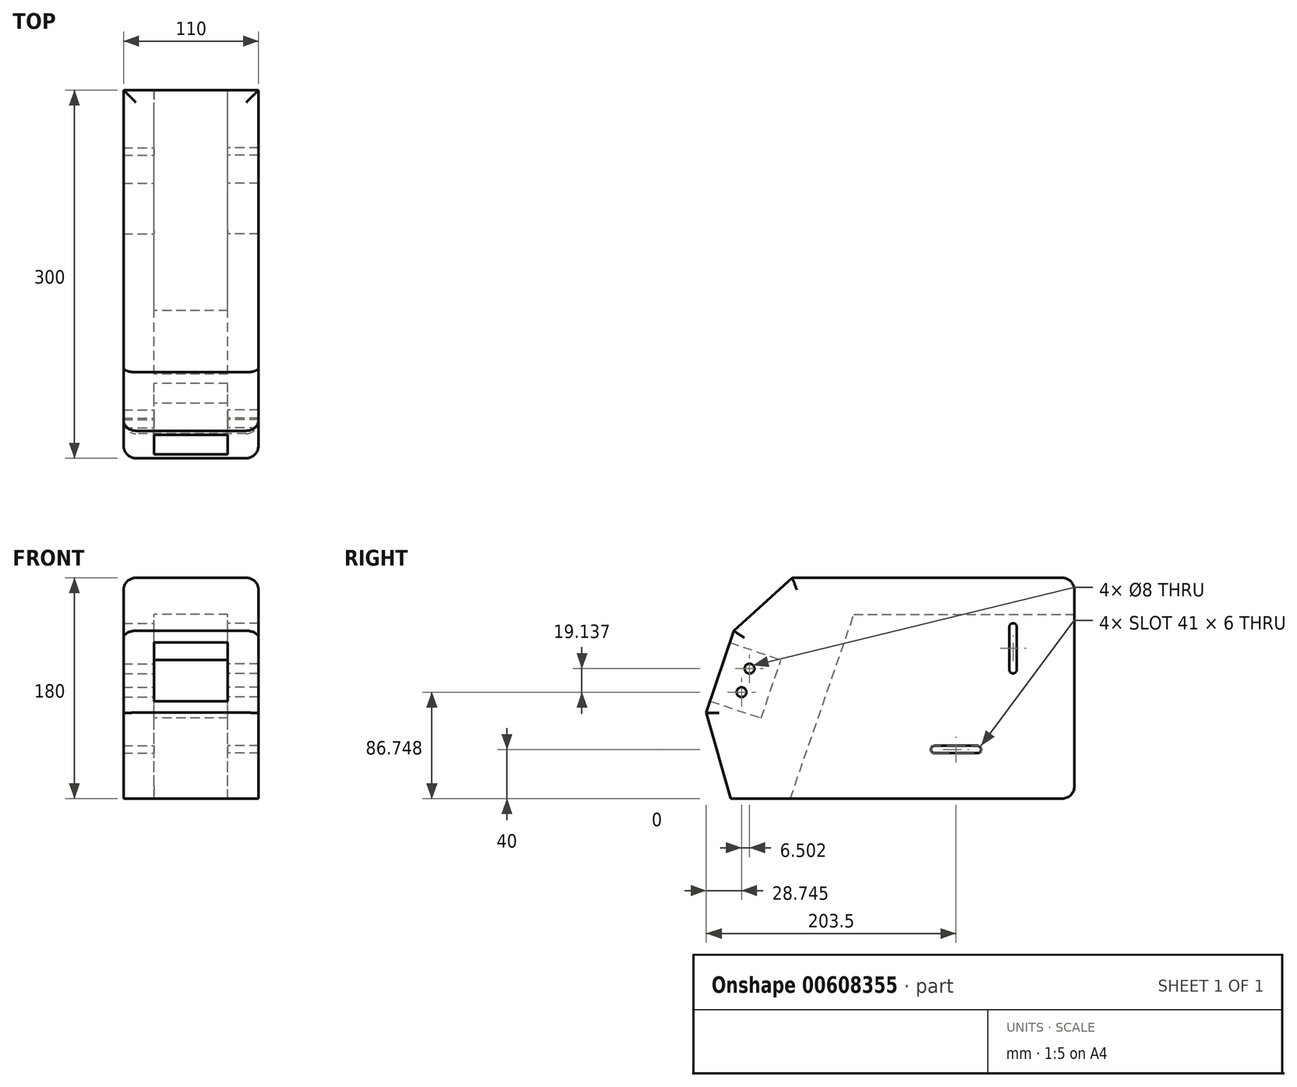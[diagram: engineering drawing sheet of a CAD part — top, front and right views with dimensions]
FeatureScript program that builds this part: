
annotation { "Feature Type Name" : "Feature", "Feature Type Description" : "" }
export const myFeature = defineFeature(function(context is Context, id is Id, definition is map)
    precondition{}
    {
        {
            var Q0;
            Q0=qCreatedBy(makeId("Right.planeOp"),FACE);
            var sketch = newSketch(context, id + "F0", { "sketchPlane" : qUnion([Q0])});
            skLineSegment(sketch, "E0.bottom", {"start": v(150, -90) * mm, "end": v(-150, -90) * mm, "construction": true});
            skLineSegment(sketch, "E0.top", {"start": v(150, 90) * mm, "end": v(-150, 90) * mm, "construction": true});
            skLineSegment(sketch, "E0.left", {"start": v(150, -90) * mm, "end": v(150, 90) * mm, "construction": true});
            skLineSegment(sketch, "E0.right", {"start": v(-150, -90) * mm, "end": v(-150, 90) * mm, "construction": true});
            skPoint(sketch, "E0.middle", {"position": v(0, 0) * mm});
            skLineSegment(sketch, "E1", {"start": v(-150, -20) * mm, "end": v(-113.22, 90) * mm, "construction": true});
            skLineSegment(sketch, "E2", {"start": v(-150, -20) * mm, "end": v(-92.1, -20) * mm, "construction": true});
            skLineSegment(sketch, "E3", {"start": v(-105.33, -24.4) * mm, "end": v(-89.02, 22.87) * mm});
            skLineSegment(sketch, "E4", {"start": v(-127.67, 46.79) * mm, "end": v(-130.84, 37.3) * mm});
            skLineSegment(sketch, "E5", {"start": v(-130.84, 37.3) * mm, "end": v(-89.02, 22.87) * mm});
            skLineSegment(sketch, "E6", {"start": v(-150, -20) * mm, "end": v(-146.83, -10.52) * mm});
            skLineSegment(sketch, "E7", {"start": v(-146.83, -10.52) * mm, "end": v(-105.33, -24.4) * mm});
            skLineSegment(sketch, "E8", {"start": v(-109.93, 30.09) * mm, "end": v(-126.08, -17.45) * mm, "construction": true});
            skCircle(sketch, "E9", {"center": v(-114.75, 15.89) * mm, "radius": 4 * mm, "construction": true});
            skCircle(sketch, "E10", {"center": v(-121.25, -3.25) * mm, "radius": 4 * mm, "construction": true});
            skLineSegment(sketch, "E11", {"start": v(-150, -20) * mm, "end": v(-130, -90) * mm});
            skLineSegment(sketch, "E12", {"start": v(-130, -90) * mm, "end": v(-81.49, -90) * mm});
            skLineSegment(sketch, "E13", {"start": v(-81.49, -90) * mm, "end": v(-29.72, 60) * mm});
            skLineSegment(sketch, "E14", {"start": v(-29.72, 60) * mm, "end": v(150, 60) * mm});
            skLineSegment(sketch, "E15", {"start": v(150, 60) * mm, "end": v(150, 90) * mm});
            skLineSegment(sketch, "E16", {"start": v(-127.67, 46.79) * mm, "end": v(-80, 90) * mm});
            skLineSegment(sketch, "E17", {"start": v(-80, 90) * mm, "end": v(150, 90) * mm});
            skLineSegment(sketch, "E18", {"start": v(-29.72, 60) * mm, "end": v(-19.36, 90) * mm});
            skLineSegment(sketch, "E19", {"start": v(-19.36, 90) * mm, "end": v(-24.54, 75) * mm});
            skSolve(sketch);
        }
        {
            var Q0;
            Q0 = qSketchRegion(id + "F0", true);
            extrude(context, id + "F1", {"entities" : qUnion([Q0]), "endBound" : BoundingType.SYMMETRIC, "depth" : 60 * mm, "offsetDistance" : 25 * mm});
        }
        {
            var Q0;
            Q0=makeQuery(id+"F1.opExtrude","CAP_FACE",FACE,{"disambiguationData":[OSD([sQuery(id+"F0.wireOp",EDGE,"E3"),sQuery(id+"F0.wireOp",EDGE,"E4"),sQuery(id+"F0.wireOp",EDGE,"E5"),sQuery(id+"F0.wireOp",EDGE,"E6"),sQuery(id+"F0.wireOp",EDGE,"E7"),sQuery(id+"F0.wireOp",EDGE,"E11"),sQuery(id+"F0.wireOp",EDGE,"E12"),sQuery(id+"F0.wireOp",EDGE,"E13"),sQuery(id+"F0.wireOp",EDGE,"E14"),sQuery(id+"F0.wireOp",EDGE,"E15"),sQuery(id+"F0.wireOp",EDGE,"E16"),sQuery(id+"F0.wireOp",EDGE,"E17")])],"isStart":false});
            var sketch = newSketch(context, id + "F2", { "sketchPlane" : qUnion([Q0])});
            skLineSegment(sketch, "E20", {"start": v(-127.67, 46.79) * mm, "end": v(-80, 90) * mm});
            skLineSegment(sketch, "E21", {"start": v(-80, 90) * mm, "end": v(150, 90) * mm});
            skLineSegment(sketch, "E22", {"start": v(150, -90) * mm, "end": v(-130, -90) * mm});
            skLineSegment(sketch, "E23", {"start": v(-130, -90) * mm, "end": v(-150, -20) * mm});
            skLineSegment(sketch, "E24", {"start": v(-150, -20) * mm, "end": v(-127.67, 46.79) * mm});
            skLineSegment(sketch, "E25", {"start": v(36, -50) * mm, "end": v(71, -50) * mm, "construction": true});
            skLineSegment(sketch, "E26", {"start": v(71, -50) * mm, "end": v(100, -50) * mm, "construction": true});
            skLineSegment(sketch, "E27", {"start": v(100, -50) * mm, "end": v(100, 15) * mm, "construction": true});
            skLineSegment(sketch, "E28", {"start": v(100, 15) * mm, "end": v(100, 50) * mm, "construction": true});
            skLineSegment(sketch, "E29", {"start": v(150, 90) * mm, "end": v(150, -90) * mm});
            skArc(sketch, "E30.0.startCap", {"start": v(103, 15) * mm, "mid": v(100, 12) * mm, "end": v(97, 15) * mm});
            skArc(sketch, "E30.0.endCap", {"start": v(97, 50) * mm, "mid": v(100, 53) * mm, "end": v(103, 50) * mm});
            skLineSegment(sketch, "E30.0.left", {"start": v(97, 15) * mm, "end": v(97, 50) * mm});
            skLineSegment(sketch, "E30.0.right", {"start": v(103, 15) * mm, "end": v(103, 50) * mm});
            skArc(sketch, "E31.0.startCap", {"start": v(36, -53) * mm, "mid": v(33, -50) * mm, "end": v(36, -47) * mm});
            skArc(sketch, "E31.0.endCap", {"start": v(71, -47) * mm, "mid": v(74, -50) * mm, "end": v(71, -53) * mm});
            skLineSegment(sketch, "E31.0.left", {"start": v(36, -47) * mm, "end": v(71, -47) * mm});
            skLineSegment(sketch, "E31.0.right", {"start": v(36, -53) * mm, "end": v(71, -53) * mm});
            skCircle(sketch, "E32.0", {"center": v(-114.75, 15.89) * mm, "radius": 4 * mm});
            skCircle(sketch, "E32.1", {"center": v(-121.25, -3.25) * mm, "radius": 4 * mm});
            skSolve(sketch);
        }
        {
            var Q0;
            Q0 = qSketchRegion(id + "F2", true);
            extrude(context, id + "F3", {"entities" : qUnion([Q0]), "operationType" : NewBodyOperationType.ADD, "depth" : 25 * mm, "offsetDistance" : 25 * mm});
        }
        {
            var Q0;
            Q0=makeQuery(id+"F1.opExtrude","CAP_FACE",FACE,{"disambiguationData":[OSD([sQuery(id+"F0.wireOp",EDGE,"E3"),sQuery(id+"F0.wireOp",EDGE,"E4"),sQuery(id+"F0.wireOp",EDGE,"E5"),sQuery(id+"F0.wireOp",EDGE,"E6"),sQuery(id+"F0.wireOp",EDGE,"E7"),sQuery(id+"F0.wireOp",EDGE,"E11"),sQuery(id+"F0.wireOp",EDGE,"E12"),sQuery(id+"F0.wireOp",EDGE,"E13"),sQuery(id+"F0.wireOp",EDGE,"E14"),sQuery(id+"F0.wireOp",EDGE,"E15"),sQuery(id+"F0.wireOp",EDGE,"E16"),sQuery(id+"F0.wireOp",EDGE,"E17")])],"isStart":true});
            var sketch = newSketch(context, id + "F4", { "sketchPlane" : qUnion([Q0])});
            skLineSegment(sketch, "E33.0.0", {"start": v(127.67, 46.79) * mm, "end": v(150, -20) * mm});
            skLineSegment(sketch, "E33.0.1", {"start": v(150, -20) * mm, "end": v(130, -90) * mm});
            skLineSegment(sketch, "E33.0.2", {"start": v(130, -90) * mm, "end": v(-150, -90) * mm});
            skLineSegment(sketch, "E33.0.3", {"start": v(-150, -90) * mm, "end": v(-150, 90) * mm});
            skLineSegment(sketch, "E33.0.4", {"start": v(-150, 90) * mm, "end": v(80, 90) * mm});
            skLineSegment(sketch, "E33.0.5", {"start": v(80, 90) * mm, "end": v(127.67, 46.79) * mm});
            skLineSegment(sketch, "E34.0", {"start": v(-103, 15) * mm, "end": v(-103, 50) * mm});
            skArc(sketch, "E34.1", {"start": v(-97, 50) * mm, "mid": v(-100, 53) * mm, "end": v(-103, 50) * mm});
            skLineSegment(sketch, "E34.2", {"start": v(-97, 15) * mm, "end": v(-97, 50) * mm});
            skArc(sketch, "E34.3", {"start": v(-103, 15) * mm, "mid": v(-100, 12) * mm, "end": v(-97, 15) * mm});
            skLineSegment(sketch, "E34.4", {"start": v(-36, -47) * mm, "end": v(-71, -47) * mm});
            skLineSegment(sketch, "E34.5", {"start": v(-36, -53) * mm, "end": v(-71, -53) * mm});
            skArc(sketch, "E34.6", {"start": v(-71, -47) * mm, "mid": v(-74, -50) * mm, "end": v(-71, -53) * mm});
            skArc(sketch, "E34.7", {"start": v(-36, -53) * mm, "mid": v(-33, -50) * mm, "end": v(-36, -47) * mm});
            skSolve(sketch);
        }
        {
            var Q0;
            Q0=makeQuery(id+"F4.imprint","IMPRINT",FACE,{"disambiguationData":[TD([[makeQuery(id+"F4.imprint","IMPRINT",EDGE,{"derivedFrom":sQuery(id+"F4.wireOp",EDGE,"E34.0")}),1.0]])]});
            var Q1;
            {var subQ7=sQuery(id+"F4.wireOp",EDGE,"E33.0.1");Q1=makeQuery(id+"F4.imprint","IMPRINT",FACE,{"disambiguationData":[TD([[makeQuery(id+"F4.imprint","IMPRINT",EDGE,{"derivedFrom":subQ7}),-1.0]])]});}
            var Q2;
            Q2=makeQuery(id+"F4.imprint","IMPRINT",FACE,{"disambiguationData":[TD([[makeQuery(id+"F4.imprint","IMPRINT",EDGE,{"derivedFrom":makeQuery(id+"F1.opExtrude","CAP_EDGE",EDGE,{"disambiguationData":[OSD([sQuery(id+"F0.wireOp",EDGE,"E3")])],"isStart":true})}),-1.0]])]});
            extrude(context, id + "F5", {"entities" : qUnion([Q0, Q1, Q2]), "operationType" : NewBodyOperationType.ADD, "depth" : 25 * mm, "offsetDistance" : 25 * mm});
        }
        {
            var Q0;
            Q0=makeQuery(id+"F3.opExtrude","CAP_EDGE",EDGE,{"disambiguationData":[OSD([sQuery(id+"F2.wireOp",EDGE,"E21")])],"isStart":false});
            var Q1;
            Q1=makeQuery(id+"F3.opExtrude","CAP_EDGE",EDGE,{"disambiguationData":[OSD([sQuery(id+"F2.wireOp",EDGE,"E20")])],"isStart":false});
            var Q2;
            Q2=makeQuery(id+"F3.opExtrude","CAP_EDGE",EDGE,{"disambiguationData":[OSD([sQuery(id+"F2.wireOp",EDGE,"E23")])],"isStart":false});
            var Q3;
            Q3=makeQuery(id+"F5.opExtrude","CAP_EDGE",EDGE,{"disambiguationData":[OSD([sQuery(id+"F4.wireOp",EDGE,"E33.0.1")])],"isStart":false});
            var Q4;
            Q4=makeQuery(id+"F5.opExtrude","CAP_EDGE",EDGE,{"disambiguationData":[OSD([sQuery(id+"F4.wireOp",EDGE,"E33.0.5")])],"isStart":false});
            var Q5;
            Q5=makeQuery(id+"F5.opExtrude","CAP_EDGE",EDGE,{"disambiguationData":[OSD([sQuery(id+"F4.wireOp",EDGE,"E33.0.4")])],"isStart":false});
            var Q6;
            Q6=makeQuery(id+"F5.boolean.opBoolean","MERGE",EDGE,{"derivedFrom":[makeQuery(id+"F3.boolean.opBoolean","MERGE",EDGE,{"derivedFrom":[makeQuery(id+"F1.opExtrude","SWEPT_EDGE",EDGE,{"disambiguationData":[OSD([sQuery(id+"F0.wireOp",EDGE,"E15"),sQuery(id+"F0.wireOp",EDGE,"E17")])]}),makeQuery(id+"F3.opExtrude","SWEPT_EDGE",EDGE,{"disambiguationData":[OSD([sQuery(id+"F2.wireOp",EDGE,"E21"),sQuery(id+"F2.wireOp",EDGE,"E29")])]})]}),makeQuery(id+"F5.opExtrude","SWEPT_EDGE",EDGE,{"disambiguationData":[OSD([sQuery(id+"F4.wireOp",EDGE,"E33.0.3"),sQuery(id+"F4.wireOp",EDGE,"E33.0.4")])]})]});
            var Q7;
            Q7=makeQuery(id+"F5.opExtrude","SWEPT_EDGE",EDGE,{"disambiguationData":[OSD([sQuery(id+"F4.wireOp",EDGE,"E33.0.2"),sQuery(id+"F4.wireOp",EDGE,"E33.0.3")])]});
            var Q8;
            Q8=makeQuery(id+"F3.opExtrude","SWEPT_EDGE",EDGE,{"disambiguationData":[OSD([sQuery(id+"F2.wireOp",EDGE,"E22"),sQuery(id+"F2.wireOp",EDGE,"E29")])]});
            var Q9;
            Q9=makeQuery(id+"F5.opExtrude","CAP_EDGE",EDGE,{"disambiguationData":[OSD([sQuery(id+"F4.wireOp",EDGE,"E33.0.0")])],"isStart":false});
            var Q10;
            Q10=makeQuery(id+"F3.opExtrude","CAP_EDGE",EDGE,{"disambiguationData":[OSD([sQuery(id+"F2.wireOp",EDGE,"E24")])],"isStart":false});
            fillet(context, id + "F6", {"entities" : qUnion([Q0, Q1, Q2, Q3, Q4, Q5, Q6, Q7, Q8, Q9, Q10]), "radius" : 10 * mm, "tangentPropagation" : true, "allowEdgeOverflow" : false});
        }
        {
            var Q0;
            Q0=sQuery(id+"F2.wireOp",VERTEX,"E32.0.center");
            var Q1;
            Q1=sQuery(id+"F2.wireOp",VERTEX,"E32.1.center");
            var Q2;
            Q2=makeQuery(id+"F1.opExtrude","SWEPT_BODY",BODY,{"disambiguationData":[OSD([sQuery(id+"F0.wireOp",EDGE,"E3"),sQuery(id+"F0.wireOp",EDGE,"E4"),sQuery(id+"F0.wireOp",EDGE,"E5"),sQuery(id+"F0.wireOp",EDGE,"E6"),sQuery(id+"F0.wireOp",EDGE,"E7"),sQuery(id+"F0.wireOp",EDGE,"E11"),sQuery(id+"F0.wireOp",EDGE,"E12"),sQuery(id+"F0.wireOp",EDGE,"E13"),sQuery(id+"F0.wireOp",EDGE,"E14"),sQuery(id+"F0.wireOp",EDGE,"E15"),sQuery(id+"F0.wireOp",EDGE,"E16"),sQuery(id+"F0.wireOp",EDGE,"E17")])]});
            hole(context, id + "F7", {"style" : HoleStyle.SIMPLE, "endStyle" : HoleEndStyle.THROUGH, "holeDiameter" : 8 * mm, "majorDiameter" : 5 * mm, "isTappedThrough" : true, "tappedDepth" : 12 * mm, "tapClearance" : 3, "locations" : qUnion([Q0, Q1]), "scope" : qUnion([Q2])});
        }
    });
